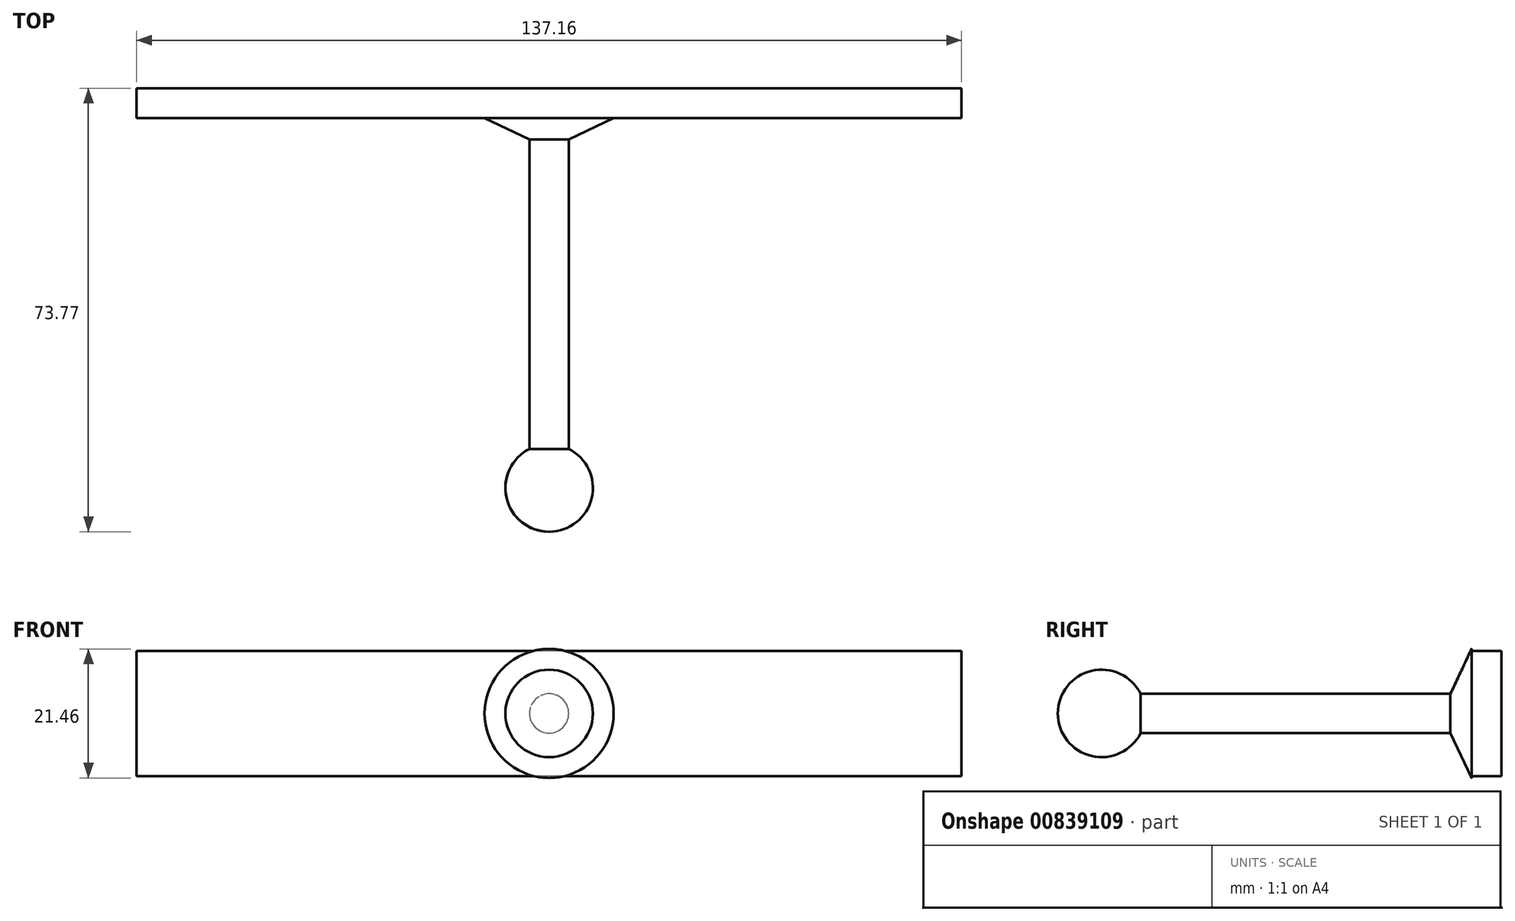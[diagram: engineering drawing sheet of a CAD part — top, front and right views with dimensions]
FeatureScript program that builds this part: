
annotation { "Feature Type Name" : "Feature", "Feature Type Description" : "" }
export const myFeature = defineFeature(function(context is Context, id is Id, definition is map)
    precondition{}
    {
        {
            var Q0;
            Q0=qCreatedBy(makeId("Top.planeOp"),FACE);
            var sketch = newSketch(context, id + "F0", { "sketchPlane" : qUnion([Q0])});
            skArc(sketch, "E0", {"start": v(0, -34.33) * mm, "mid": v(-7.28, -41.6) * mm, "end": v(0, -48.88) * mm});
            skLineSegment(sketch, "E1", {"start": v(0, -34.33) * mm, "end": v(0, -48.88) * mm});
            skLineSegment(sketch, "E2", {"start": v(-3.26, -35.1) * mm, "end": v(-3.26, 16.4) * mm});
            skLineSegment(sketch, "E3", {"start": v(-3.26, 16.4) * mm, "end": v(0, 16.4) * mm});
            skLineSegment(sketch, "E4", {"start": v(0, 16.4) * mm, "end": v(0, -34.33) * mm});
            skLineSegment(sketch, "E5", {"start": v(-3.26, 16.4) * mm, "end": v(-10.73, 19.9) * mm});
            skLineSegment(sketch, "E6", {"start": v(-10.73, 19.9) * mm, "end": v(0, 19.9) * mm});
            skLineSegment(sketch, "E7", {"start": v(0, 19.9) * mm, "end": v(0, 16.4) * mm});
            skLineSegment(sketch, "E8.bottom", {"start": v(0, 19.9) * mm, "end": v(-10.73, 19.9) * mm});
            skLineSegment(sketch, "E9.bottom", {"start": v(0, 19.9) * mm, "end": v(-68.58, 19.9) * mm});
            skLineSegment(sketch, "E9.top", {"start": v(0, 24.9) * mm, "end": v(-68.58, 24.9) * mm});
            skLineSegment(sketch, "E9.right", {"start": v(-68.58, 19.9) * mm, "end": v(-68.58, 24.9) * mm});
            skLineSegment(sketch, "E10.bottom", {"start": v(0, 24.9) * mm, "end": v(68.58, 24.9) * mm});
            skLineSegment(sketch, "E10.top", {"start": v(0, 19.9) * mm, "end": v(68.58, 19.9) * mm});
            skLineSegment(sketch, "E10.left", {"start": v(0, 24.9) * mm, "end": v(0, 19.9) * mm});
            skLineSegment(sketch, "E10.right", {"start": v(68.58, 24.9) * mm, "end": v(68.58, 19.9) * mm});
            skSolve(sketch);
        }
        {
            var Q0;
            Q0=makeQuery(id+"F0.imprint","IMPRINT",FACE,{"disambiguationData":[TD([[makeQuery(id+"F0.imprint","IMPRINT",EDGE,{"derivedFrom":sQuery(id+"F0.wireOp",EDGE,"E3")}),1.0]])]});
            var Q1;
            {var subQ2=sQuery(id+"F0.wireOp",EDGE,"E2");Q1=makeQuery(id+"F0.imprint","IMPRINT",FACE,{"disambiguationData":[TD([[makeQuery(id+"F0.imprint","IMPRINT",EDGE,{"derivedFrom":subQ2}),-1.0]])]});}
            var Q2;
            {var subQ0=sQuery(id+"F0.wireOp",EDGE,"E1");Q2=makeQuery(id+"F0.imprint","IMPRINT",FACE,{"disambiguationData":[TD([[makeQuery(id+"F0.imprint","IMPRINT",EDGE,{"derivedFrom":subQ0}),-1.0]])]});}
            var Q3;
            Q3=sQuery(id+"F0.wireOp",EDGE,"E4");
            revolve(context, id + "F1", {"surfaceOperationType" : NewSurfaceOperationType.NEW, "entities" : qUnion([Q0, Q1, Q2]), "axis" : qUnion([Q3]), "revolveType" : RevolveType.FULL});
        }
        {
            var Q0;
            Q0=makeQuery(id+"F0.imprint","IMPRINT",FACE,{"disambiguationData":[TD([[makeQuery(id+"F0.imprint","IMPRINT",EDGE,{"derivedFrom":sQuery(id+"F0.wireOp",EDGE,"E9.top")}),1.0]])]});
            var Q1;
            Q1=makeQuery(id+"F0.imprint","IMPRINT",FACE,{"disambiguationData":[TD([[makeQuery(id+"F0.imprint","IMPRINT",EDGE,{"derivedFrom":sQuery(id+"F0.wireOp",EDGE,"E10.bottom")}),-1.0]])]});
            extrude(context, id + "F2", {"entities" : qUnion([Q0, Q1]), "operationType" : NewBodyOperationType.ADD, "endBound" : BoundingType.SYMMETRIC, "depth" : 20.83 * mm, "offsetDistance" : 25.4 * mm});
        }
    });
